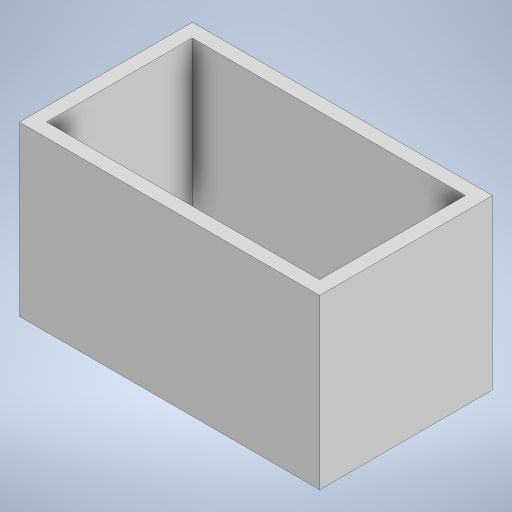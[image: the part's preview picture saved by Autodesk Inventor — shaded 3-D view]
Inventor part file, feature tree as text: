
AUTODESK INVENTOR PART (.ipt)
format: ipt  version: 2023 (Build 270158000, 158)  size: 239,104 bytes
history: native  units: mm
features: extrude x6, sketch x5, other x1
ambient origin geometry x8: Origin, YZ Plane, XZ Plane, XY Plane, X Axis, Y Axis, Z Axis, Center Point
bodies: Body1 (feature_tree)
feature tree (12):
  other  "솔리드1"
  sketch  "스케치1"
  extrude  "돌출1"  Depth=60.0mm
  extrude  "돌출2"  Depth=32.0mm
  extrude  "돌출3"  Depth=3.0mm
  extrude  "돌출4"  Depth=3.0mm TaperAngle=0.0deg
  extrude  "돌출5"  Depth=34.0mm TaperAngle=0.0deg
  extrude  "돌출6"  Depth=2.0mm
  sketch  "스케치2"
  sketch  "스케치3"
  sketch  "스케치4"
  sketch  "스케치5"
